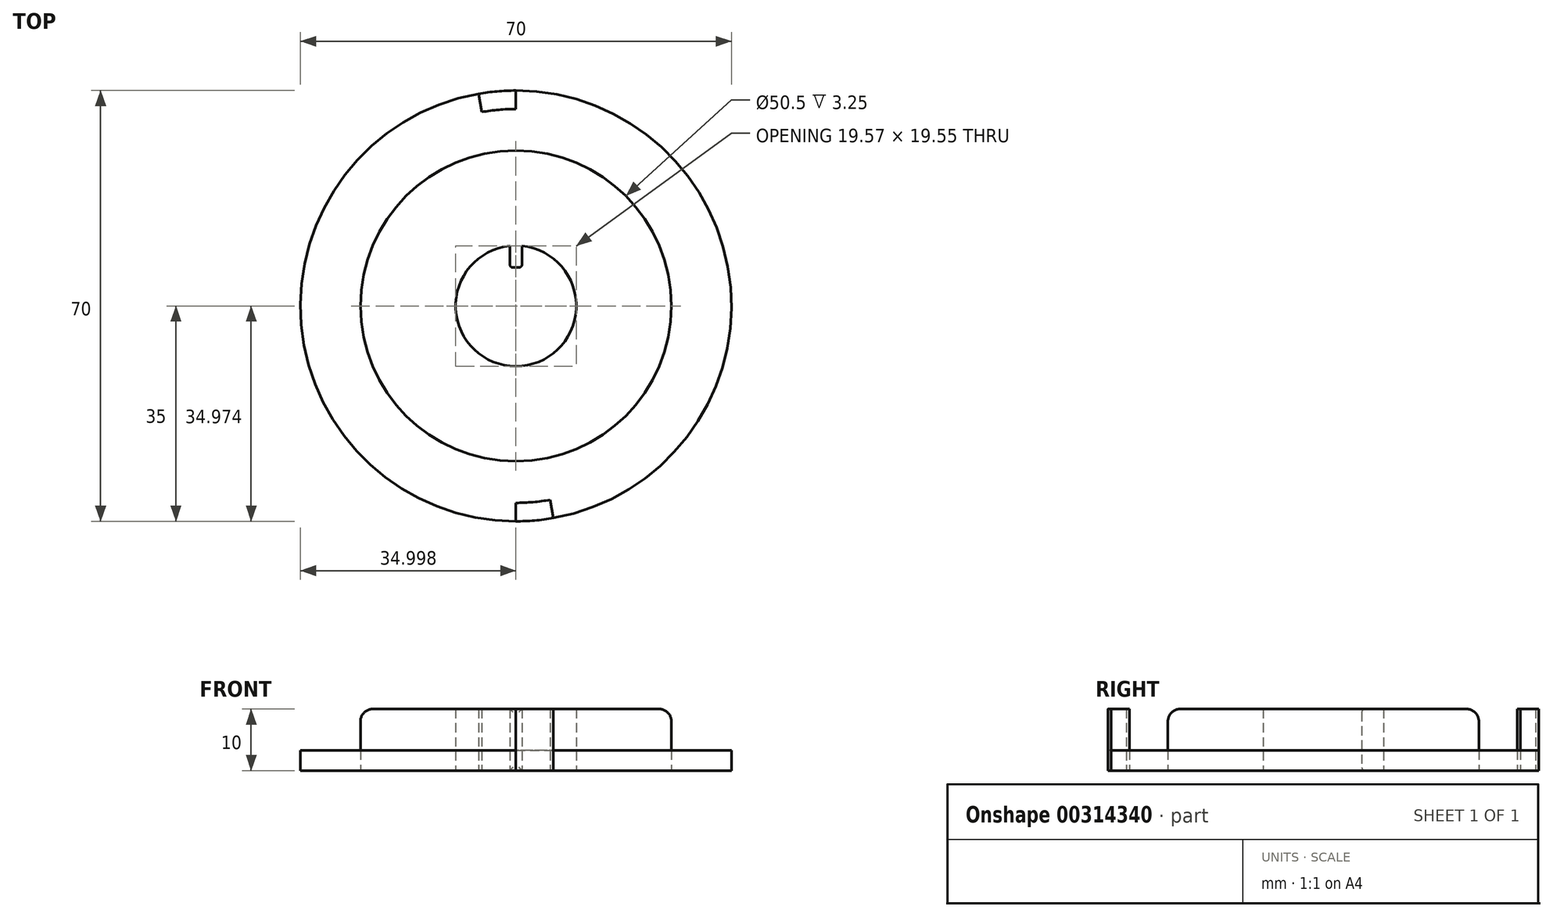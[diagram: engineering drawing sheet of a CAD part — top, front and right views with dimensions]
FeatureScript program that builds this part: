
annotation { "Feature Type Name" : "Feature", "Feature Type Description" : "" }
export const myFeature = defineFeature(function(context is Context, id is Id, definition is map)
    precondition{}
    {
        {
            var Q0;
            Q0=qCreatedBy(makeId("Top.planeOp"),FACE);
            var sketch = newSketch(context, id + "F0", { "sketchPlane" : qUnion([Q0])});
            skCircle(sketch, "E0", {"center": v(0, 0) * mm, "radius": 25.25 * mm});
            skCircle(sketch, "E1", {"center": v(0, 0) * mm, "radius": 9.8 * mm});
            skCircle(sketch, "E2", {"center": v(0, 0) * mm, "radius": 35 * mm});
            skCircle(sketch, "E3", {"center": v(0, 0) * mm, "radius": 32 * mm});
            skLineSegment(sketch, "E4", {"start": v(0, 0) * mm, "end": v(0, 35) * mm});
            skLineSegment(sketch, "E5", {"start": v(0, 0) * mm, "end": v(0, -35) * mm});
            skLineSegment(sketch, "E6", {"start": v(0, 0) * mm, "end": v(-6.08, 34.47) * mm});
            skLineSegment(sketch, "E7", {"start": v(0, 0) * mm, "end": v(6.08, -34.47) * mm});
            skLineSegment(sketch, "E8", {"start": v(-1, 9.75) * mm, "end": v(-1, 6.25) * mm});
            skLineSegment(sketch, "E9", {"start": v(-1, 6.25) * mm, "end": v(1, 6.25) * mm});
            skLineSegment(sketch, "E10", {"start": v(1, 6.25) * mm, "end": v(1, 9.75) * mm});
            skSolve(sketch);
        }
        {
            var Q0;
            {var subQ0=sQuery(id+"F0.wireOp",EDGE,"E6");var subQ1=sQuery(id+"F0.wireOp",EDGE,"E0");var subQ2=makeQuery(id+"F0.imprint","INTERSECT",VERTEX,{"derivedFrom":[subQ1,subQ0]});Q0=makeQuery(id+"F0.imprint","IMPRINT",FACE,{"disambiguationData":[TD([[makeQuery(id+"F0.imprint","IMPRINT",EDGE,{"disambiguationData":[TD([[subQ2,-1.0]])],"derivedFrom":subQ1}),1.0]])]});}
            var Q1;
            {var subQ2=sQuery(id+"F0.wireOp",EDGE,"E6");var subQ4=sQuery(id+"F0.wireOp",EDGE,"E0");var subQ5=makeQuery(id+"F0.imprint","INTERSECT",VERTEX,{"derivedFrom":[subQ4,subQ2]});Q1=makeQuery(id+"F0.imprint","IMPRINT",FACE,{"disambiguationData":[TD([[makeQuery(id+"F0.imprint","IMPRINT",EDGE,{"disambiguationData":[TD([[subQ5,1.0]])],"derivedFrom":subQ4}),1.0]])]});}
            var Q2;
            {var subQ0=sQuery(id+"F0.wireOp",EDGE,"E4");var subQ1=sQuery(id+"F0.wireOp",EDGE,"E0");var subQ2=makeQuery(id+"F0.imprint","INTERSECT",VERTEX,{"derivedFrom":[subQ1,subQ0]});Q2=makeQuery(id+"F0.imprint","IMPRINT",FACE,{"disambiguationData":[TD([[makeQuery(id+"F0.imprint","IMPRINT",EDGE,{"disambiguationData":[TD([[subQ2,1.0]])],"derivedFrom":subQ1}),1.0]])]});}
            var Q3;
            {var subQ0=sQuery(id+"F0.wireOp",EDGE,"E5");var subQ1=sQuery(id+"F0.wireOp",EDGE,"E0");var subQ2=makeQuery(id+"F0.imprint","INTERSECT",VERTEX,{"derivedFrom":[subQ1,subQ0]});Q3=makeQuery(id+"F0.imprint","IMPRINT",FACE,{"disambiguationData":[TD([[makeQuery(id+"F0.imprint","IMPRINT",EDGE,{"disambiguationData":[TD([[subQ2,-1.0]])],"derivedFrom":subQ1}),1.0]])]});}
            var Q4;
            {var subQ0=sQuery(id+"F0.wireOp",EDGE,"E10");Q4=makeQuery(id+"F0.imprint","IMPRINT",FACE,{"disambiguationData":[TD([[makeQuery(id+"F0.imprint","IMPRINT",EDGE,{"derivedFrom":subQ0}),1.0]])]});}
            var Q5;
            {var subQ0=sQuery(id+"F0.wireOp",EDGE,"E8");Q5=makeQuery(id+"F0.imprint","IMPRINT",FACE,{"disambiguationData":[TD([[makeQuery(id+"F0.imprint","IMPRINT",EDGE,{"derivedFrom":subQ0}),1.0]])]});}
            var Q6;
            {var subQ0=sQuery(id+"F0.wireOp",EDGE,"E4");var subQ1=sQuery(id+"F0.wireOp",EDGE,"E2");var subQ2=makeQuery(id+"F0.imprint","INTERSECT",VERTEX,{"derivedFrom":[subQ1,subQ0]});Q6=makeQuery(id+"F0.imprint","IMPRINT",FACE,{"disambiguationData":[TD([[makeQuery(id+"F0.imprint","IMPRINT",EDGE,{"disambiguationData":[TD([[subQ2,-1.0]])],"derivedFrom":subQ1}),1.0]])]});}
            var Q7;
            {var subQ0=sQuery(id+"F0.wireOp",EDGE,"E5");var subQ1=sQuery(id+"F0.wireOp",EDGE,"E2");var subQ2=makeQuery(id+"F0.imprint","INTERSECT",VERTEX,{"derivedFrom":[subQ1,subQ0]});Q7=makeQuery(id+"F0.imprint","IMPRINT",FACE,{"disambiguationData":[TD([[makeQuery(id+"F0.imprint","IMPRINT",EDGE,{"disambiguationData":[TD([[subQ2,-1.0]])],"derivedFrom":subQ1}),1.0]])]});}
            extrude(context, id + "F1", {"entities" : qUnion([Q0, Q1, Q2, Q3, Q4, Q5, Q6, Q7]), "depth" : 10 * mm});
        }
        {
            var Q0;
            {var subQ0=sQuery(id+"F0.wireOp",EDGE,"E6");var subQ1=sQuery(id+"F0.wireOp",EDGE,"E0");var subQ2=makeQuery(id+"F0.imprint","INTERSECT",VERTEX,{"derivedFrom":[subQ1,subQ0]});Q0=makeQuery(id+"F0.imprint","IMPRINT",FACE,{"disambiguationData":[TD([[makeQuery(id+"F0.imprint","IMPRINT",EDGE,{"disambiguationData":[TD([[subQ2,-1.0]])],"derivedFrom":subQ1}),-1.0]])]});}
            var Q1;
            {var subQ0=sQuery(id+"F0.wireOp",EDGE,"E5");var subQ1=sQuery(id+"F0.wireOp",EDGE,"E2");var subQ2=makeQuery(id+"F0.imprint","INTERSECT",VERTEX,{"derivedFrom":[subQ1,subQ0]});Q1=makeQuery(id+"F0.imprint","IMPRINT",FACE,{"disambiguationData":[TD([[makeQuery(id+"F0.imprint","IMPRINT",EDGE,{"disambiguationData":[TD([[subQ2,1.0]])],"derivedFrom":subQ1}),1.0]])]});}
            var Q2;
            {var subQ0=sQuery(id+"F0.wireOp",EDGE,"E6");var subQ1=sQuery(id+"F0.wireOp",EDGE,"E0");var subQ2=makeQuery(id+"F0.imprint","INTERSECT",VERTEX,{"derivedFrom":[subQ1,subQ0]});Q2=makeQuery(id+"F0.imprint","IMPRINT",FACE,{"disambiguationData":[TD([[makeQuery(id+"F0.imprint","IMPRINT",EDGE,{"disambiguationData":[TD([[subQ2,1.0]])],"derivedFrom":subQ1}),-1.0]])]});}
            var Q3;
            {var subQ0=sQuery(id+"F0.wireOp",EDGE,"E4");var subQ1=sQuery(id+"F0.wireOp",EDGE,"E2");var subQ2=makeQuery(id+"F0.imprint","INTERSECT",VERTEX,{"derivedFrom":[subQ1,subQ0]});Q3=makeQuery(id+"F0.imprint","IMPRINT",FACE,{"disambiguationData":[TD([[makeQuery(id+"F0.imprint","IMPRINT",EDGE,{"disambiguationData":[TD([[subQ2,1.0]])],"derivedFrom":subQ1}),1.0]])]});}
            var Q4;
            {var subQ0=sQuery(id+"F0.wireOp",EDGE,"E4");var subQ1=sQuery(id+"F0.wireOp",EDGE,"E0");var subQ2=makeQuery(id+"F0.imprint","INTERSECT",VERTEX,{"derivedFrom":[subQ1,subQ0]});Q4=makeQuery(id+"F0.imprint","IMPRINT",FACE,{"disambiguationData":[TD([[makeQuery(id+"F0.imprint","IMPRINT",EDGE,{"disambiguationData":[TD([[subQ2,1.0]])],"derivedFrom":subQ1}),-1.0]])]});}
            var Q5;
            {var subQ0=sQuery(id+"F0.wireOp",EDGE,"E5");var subQ1=sQuery(id+"F0.wireOp",EDGE,"E0");var subQ2=makeQuery(id+"F0.imprint","INTERSECT",VERTEX,{"derivedFrom":[subQ1,subQ0]});Q5=makeQuery(id+"F0.imprint","IMPRINT",FACE,{"disambiguationData":[TD([[makeQuery(id+"F0.imprint","IMPRINT",EDGE,{"disambiguationData":[TD([[subQ2,-1.0]])],"derivedFrom":subQ1}),-1.0]])]});}
            extrude(context, id + "F2", {"entities" : qUnion([Q0, Q1, Q2, Q3, Q4, Q5]), "depth" : 3.25 * mm});
        }
        {
            var Q0;
            Q0=makeQuery(id+"F1.opExtrude","CAP_EDGE",EDGE,{"disambiguationData":[OSD([sQuery(id+"F0.wireOp",EDGE,"E0")])],"isStart":false});
            fillet(context, id + "F3", {"entities" : qUnion([Q0]), "radius" : 2 * mm, "tangentPropagation" : true, "allowEdgeOverflow" : false});
        }
        {
            var Q0;
            Q0=makeQuery(id+"F1.opExtrude","SWEPT_EDGE",EDGE,{"disambiguationData":[OSD([sQuery(id+"F0.wireOp",EDGE,"E9"),sQuery(id+"F0.wireOp",EDGE,"E10")])]});
            var Q1;
            Q1=makeQuery(id+"F1.opExtrude","SWEPT_EDGE",EDGE,{"disambiguationData":[OSD([sQuery(id+"F0.wireOp",EDGE,"E8"),sQuery(id+"F0.wireOp",EDGE,"E9")])]});
            var Q2;
            Q2=makeQuery(id+"F1.opExtrude","CAP_EDGE",EDGE,{"disambiguationData":[OSD([sQuery(id+"F0.wireOp",EDGE,"E9")])],"isStart":false});
            var Q3;
            Q3=makeQuery(id+"F1.opExtrude","CAP_EDGE",EDGE,{"disambiguationData":[OSD([sQuery(id+"F0.wireOp",EDGE,"E9")])],"isStart":true});
            fillet(context, id + "F4", {"entities" : qUnion([Q0, Q1, Q2, Q3]), "radius" : 0.5 * mm, "tangentPropagation" : true, "allowEdgeOverflow" : false});
        }
    });
